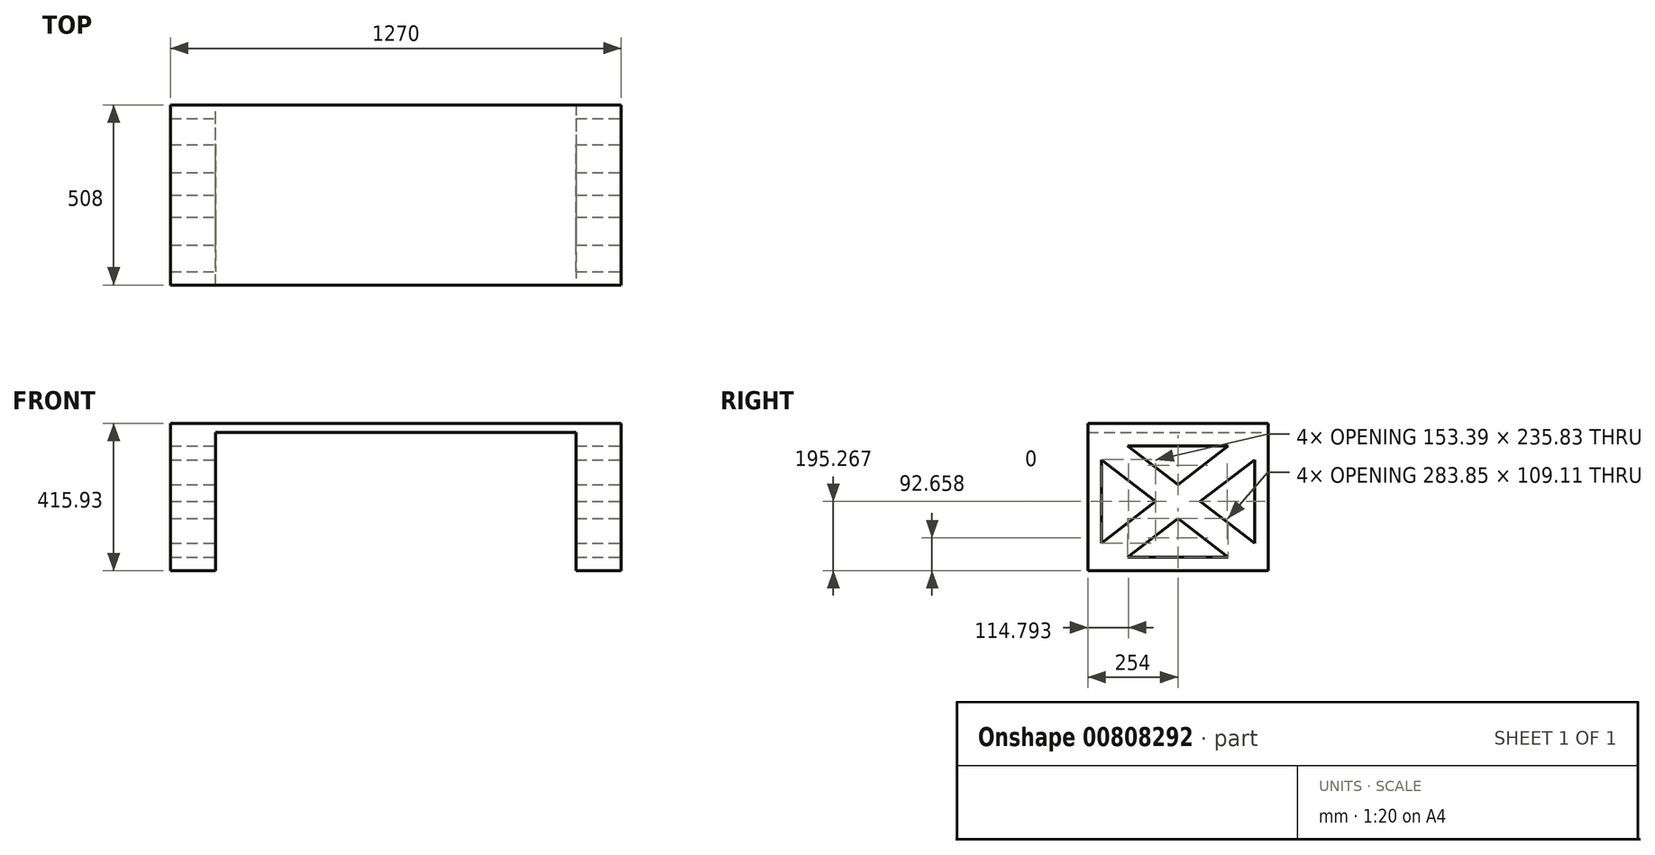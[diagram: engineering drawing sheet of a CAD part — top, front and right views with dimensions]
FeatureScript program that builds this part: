
annotation { "Feature Type Name" : "Feature", "Feature Type Description" : "" }
export const myFeature = defineFeature(function(context is Context, id is Id, definition is map)
    precondition{}
    {
        {
            var Q0;
            Q0=qCreatedBy(makeId("Top.planeOp"),FACE);
            var sketch = newSketch(context, id + "F0", { "sketchPlane" : qUnion([Q0])});
            skLineSegment(sketch, "E0.bottom", {"start": v(635, -254) * mm, "end": v(-635, -254) * mm});
            skLineSegment(sketch, "E0.top", {"start": v(635, 254) * mm, "end": v(-635, 254) * mm});
            skLineSegment(sketch, "E0.left", {"start": v(635, -254) * mm, "end": v(635, 254) * mm});
            skLineSegment(sketch, "E0.right", {"start": v(-635, -254) * mm, "end": v(-635, 254) * mm});
            skPoint(sketch, "E0.middle", {"position": v(0, 0) * mm});
            skSolve(sketch);
        }
        {
            var Q0;
            Q0=qSketchRegion(id+"F0",true);
            extrude(context, id + "F1", {"entities" : qUnion([Q0]), "depth" : 25.4 * mm, "offsetDistance" : 25.4 * mm});
        }
        {
            var Q0;
            Q0=makeQuery(id+"F1.opExtrude","CAP_FACE",FACE,{"disambiguationData":[OSD([sQuery(id+"F0.wireOp",EDGE,"E0.bottom"),sQuery(id+"F0.wireOp",EDGE,"E0.top"),sQuery(id+"F0.wireOp",EDGE,"E0.left"),sQuery(id+"F0.wireOp",EDGE,"E0.right")])],"isStart":true});
            var sketch = newSketch(context, id + "F2", { "sketchPlane" : qUnion([Q0])});
            skLineSegment(sketch, "E1.bottom", {"start": v(-635, 254) * mm, "end": v(-508, 254) * mm});
            skLineSegment(sketch, "E1.top", {"start": v(-635, -254) * mm, "end": v(-508, -254) * mm});
            skLineSegment(sketch, "E1.left", {"start": v(-635, 254) * mm, "end": v(-635, -254) * mm});
            skLineSegment(sketch, "E1.right", {"start": v(-508, 254) * mm, "end": v(-508, -254) * mm});
            skLineSegment(sketch, "E2.bottom", {"start": v(635, -254) * mm, "end": v(508, -254) * mm});
            skLineSegment(sketch, "E2.top", {"start": v(635, 254) * mm, "end": v(508, 254) * mm});
            skLineSegment(sketch, "E2.left", {"start": v(635, -254) * mm, "end": v(635, 254) * mm});
            skLineSegment(sketch, "E2.right", {"start": v(508, -254) * mm, "end": v(508, 254) * mm});
            skSolve(sketch);
        }
        {
            var Q0;
            Q0=qSketchRegion(id+"F2",true);
            extrude(context, id + "F3", {"entities" : qUnion([Q0]), "operationType" : NewBodyOperationType.ADD, "depth" : 390.52 * mm, "offsetDistance" : 25.4 * mm});
        }
        {
            var Q0;
            Q0=makeQuery(id+"F3.boolean.opBoolean","MERGE",FACE,{"derivedFrom":[makeQuery(id+"F1.opExtrude","SWEPT_FACE",FACE,{"disambiguationData":[OSD([sQuery(id+"F0.wireOp",EDGE,"E0.left")])]}),makeQuery(id+"F3.opExtrude","SWEPT_FACE",FACE,{"disambiguationData":[OSD([sQuery(id+"F2.wireOp",EDGE,"E2.left")])]})]});
            var sketch = newSketch(context, id + "F4", { "sketchPlane" : qUnion([Q0])});
            skLineSegment(sketch, "E3.bottom", {"start": v(254, -390.53) * mm, "end": v(-254, -390.53) * mm, "construction": true});
            skLineSegment(sketch, "E3.top", {"start": v(254, 0) * mm, "end": v(-254, 0) * mm, "construction": true});
            skLineSegment(sketch, "E3.left", {"start": v(254, -390.53) * mm, "end": v(254, 0) * mm, "construction": true});
            skLineSegment(sketch, "E3.right", {"start": v(-254, -390.53) * mm, "end": v(-254, 0) * mm, "construction": true});
            skPoint(sketch, "E3.middle", {"position": v(0, -195.26) * mm});
            skLineSegment(sketch, "E4", {"start": v(-254, -390.53) * mm, "end": v(0, -195.26) * mm, "construction": true});
            skLineSegment(sketch, "E5", {"start": v(0, -195.26) * mm, "end": v(254, -390.53) * mm, "construction": true});
            skLineSegment(sketch, "E6", {"start": v(0, -195.26) * mm, "end": v(254, 0) * mm, "construction": true});
            skLineSegment(sketch, "E7.0", {"start": v(-141.93, -352.43) * mm, "end": v(0, -243.32) * mm});
            skLineSegment(sketch, "E7.1", {"start": v(141.93, -352.43) * mm, "end": v(-141.93, -352.43) * mm});
            skLineSegment(sketch, "E7.2", {"start": v(0, -243.32) * mm, "end": v(141.93, -352.43) * mm});
            skLineSegment(sketch, "E8", {"start": v(-254, -195.26) * mm, "end": v(254, -195.26) * mm, "construction": true});
            skLineSegment(sketch, "E9.0", {"start": v(62.51, -195.26) * mm, "end": v(215.9, -77.35) * mm});
            skLineSegment(sketch, "E9.1", {"start": v(62.51, -195.26) * mm, "end": v(215.9, -313.18) * mm});
            skLineSegment(sketch, "E9.2", {"start": v(215.9, -313.18) * mm, "end": v(215.9, -77.35) * mm});
            skPoint(sketch, "E10.center", {"position": v(0, 0) * mm});
            skLineSegment(sketch, "E11.1.1", {"start": v(141.93, -38.1) * mm, "end": v(0, -147.2) * mm});
            skLineSegment(sketch, "E11.1.2", {"start": v(0, -147.2) * mm, "end": v(-141.93, -38.1) * mm});
            skLineSegment(sketch, "E11.1.3", {"start": v(-141.93, -38.1) * mm, "end": v(141.93, -38.1) * mm});
            skLineSegment(sketch, "E11.1.4", {"start": v(-62.51, -195.26) * mm, "end": v(-215.9, -77.35) * mm});
            skLineSegment(sketch, "E11.1.5", {"start": v(-215.9, -77.35) * mm, "end": v(-215.9, -313.18) * mm});
            skLineSegment(sketch, "E11.1.6", {"start": v(-62.51, -195.26) * mm, "end": v(-215.9, -313.18) * mm});
            skSolve(sketch);
        }
        {
            var Q0;
            Q0 = qSketchRegion(id + "F4", true);
            extrude(context, id + "F5", {"entities" : qUnion([Q0]), "operationType" : NewBodyOperationType.REMOVE, "endBound" : BoundingType.THROUGH_ALL, "oppositeDirection" : true, "depth" : 25.4 * mm, "offsetDistance" : 25.4 * mm});
        }
    });
